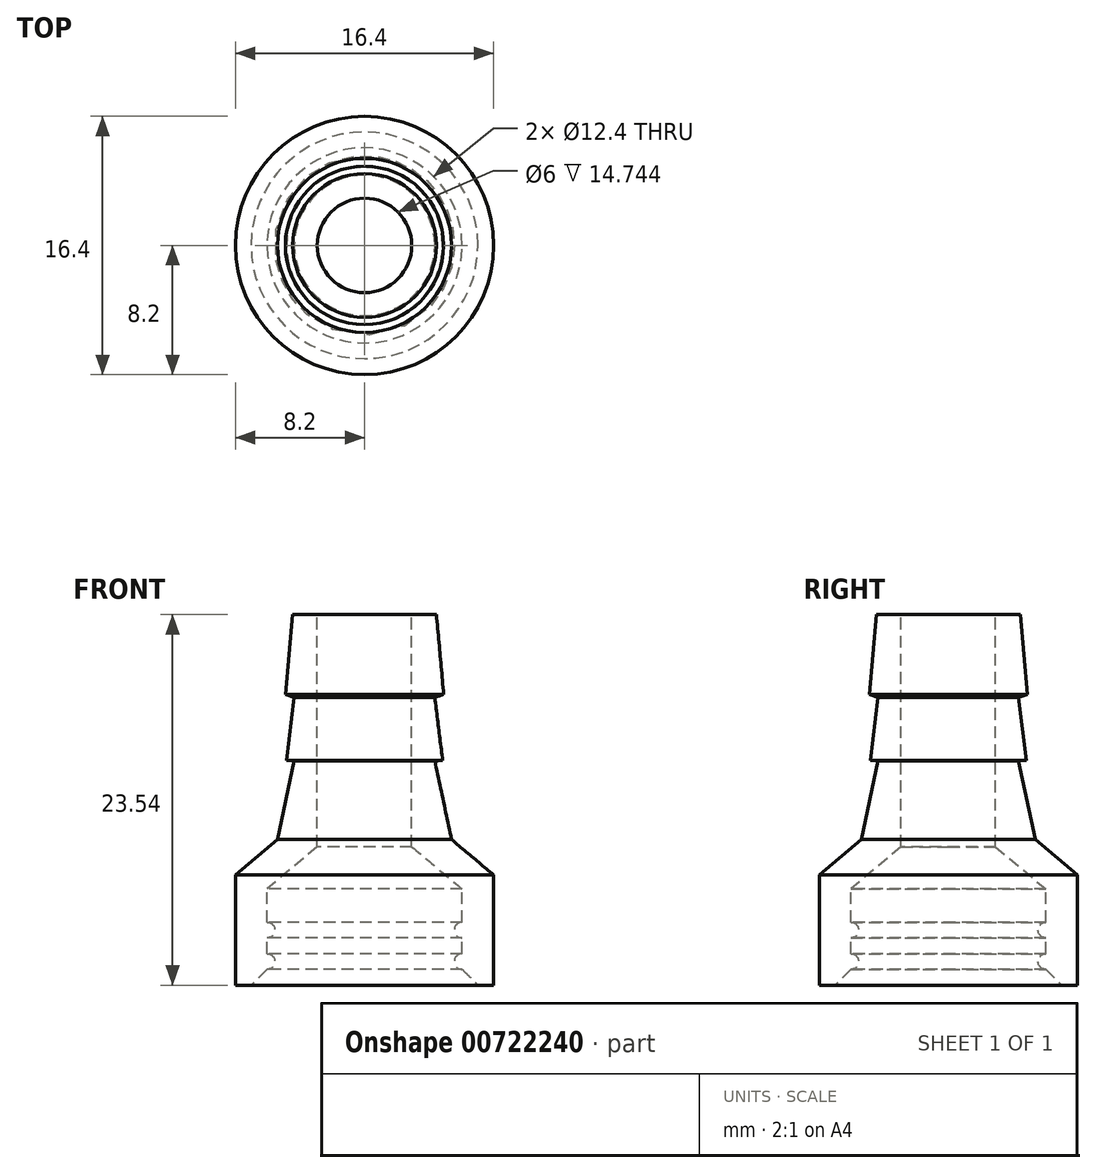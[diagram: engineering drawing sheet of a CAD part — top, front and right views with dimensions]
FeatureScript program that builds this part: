
annotation { "Feature Type Name" : "Feature", "Feature Type Description" : "" }
export const myFeature = defineFeature(function(context is Context, id is Id, definition is map)
    precondition{}
    {
        {
            var Q0;
            Q0=qCreatedBy(makeId("Front.planeOp"),FACE);
            var sketch = newSketch(context, id + "F0", { "sketchPlane" : qUnion([Q0])});
            skLineSegment(sketch, "E0", {"start": v(-6.2, -1.54) * mm, "end": v(-8.2, -1.54) * mm});
            skLineSegment(sketch, "E1", {"start": v(-8.2, -1.54) * mm, "end": v(-8.2, 5.46) * mm});
            skLineSegment(sketch, "E2", {"start": v(-6.2, -1.54) * mm, "end": v(-6.2, -0.54) * mm});
            skLineSegment(sketch, "E3", {"start": v(-3, 7.26) * mm, "end": v(-3, 22) * mm});
            skLineSegment(sketch, "E4", {"start": v(-4.57, 22) * mm, "end": v(-3, 22) * mm});
            skLineSegment(sketch, "E5", {"start": v(-4.46, 16.74) * mm, "end": v(-5.03, 16.94) * mm});
            skLineSegment(sketch, "E6", {"start": v(-4.46, 12.71) * mm, "end": v(-4.96, 12.74) * mm});
            skLineSegment(sketch, "E7", {"start": v(-4.57, 22) * mm, "end": v(-5.03, 16.94) * mm});
            skLineSegment(sketch, "E8", {"start": v(-4.46, 16.74) * mm, "end": v(-4.96, 12.74) * mm});
            skLineSegment(sketch, "E9", {"start": v(-6.2, 4.56) * mm, "end": v(-3, 7.26) * mm});
            skLineSegment(sketch, "E10", {"start": v(-4.46, 12.71) * mm, "end": v(-5.53, 7.71) * mm});
            skLineSegment(sketch, "E11", {"start": v(-8.2, 5.46) * mm, "end": v(-5.53, 7.71) * mm});
            skLineSegment(sketch, "E12.trimOffspring", {"start": v(-6.2, 2.46) * mm, "end": v(-6.2, 4.56) * mm});
            skPoint(sketch, "E13.end.orphan", {"position": v(0, 22) * mm});
            skLineSegment(sketch, "E14", {"start": v(0, 22) * mm, "end": v(0, 0) * mm});
            skLineSegment(sketch, "E15", {"start": v(-8.2, -1.54) * mm, "end": v(-5.14, -1.54) * mm, "construction": true});
            skLineSegment(sketch, "E16.0", {"start": v(-6.2, -1.54) * mm, "end": v(-6.2, -0.54) * mm, "construction": true});
            skArc(sketch, "E17", {"start": v(-6.2, -0.54) * mm, "mid": v(-5.7, -0.04) * mm, "end": v(-6.2, 0.46) * mm});
            skPoint(sketch, "E17.second.point", {"position": v(-6.2, -0.54) * mm});
            skPoint(sketch, "E17.third.point", {"position": v(-5.7, 0) * mm});
            skArc(sketch, "E18", {"start": v(-6.2, 1.46) * mm, "mid": v(-5.7, 1.96) * mm, "end": v(-6.2, 2.46) * mm});
            skPoint(sketch, "E18.first.point", {"position": v(-6.2, 2.46) * mm});
            skPoint(sketch, "E18.third.point", {"position": v(-5.7, 1.97) * mm});
            skLineSegment(sketch, "E19", {"start": v(-6.2, 1.46) * mm, "end": v(-6.2, 0.46) * mm});
            skLineSegment(sketch, "E20.trimOffspring", {"start": v(-6.2, 2.46) * mm, "end": v(-6.2, 4.56) * mm, "construction": true});
            skLineSegment(sketch, "E21.trimOffspring", {"start": v(-6.2, 0.46) * mm, "end": v(-6.2, 1.46) * mm, "construction": true});
            skSolve(sketch);
        }
        {
            var Q0;
            Q0=makeQuery(id+"F0.imprint","IMPRINT",FACE,{"disambiguationData":[TD([[makeQuery(id+"F0.imprint","IMPRINT",EDGE,{"derivedFrom":sQuery(id+"F0.wireOp",EDGE,"E0")}),-1.0]])]});
            var Q1;
            Q1=sQuery(id+"F0.wireOp",EDGE,"E14");
            revolve(context, id + "F1", {"surfaceOperationType" : NewSurfaceOperationType.NEW, "entities" : qUnion([Q0]), "axis" : qUnion([Q1]), "revolveType" : RevolveType.FULL});
        }
        {
            var Q0;
            Q0=makeQuery(id+"F1.opRevolve","SWEPT_EDGE",EDGE,{"disambiguationData":[OSD([sQuery(id+"F0.wireOp",EDGE,"E0"),sQuery(id+"F0.wireOp",EDGE,"E2")])]});
            chamfer(context, id + "F2", {"entities" : qUnion([Q0]), "width" : 1 * mm, "tangentPropagation" : true});
        }
    });
